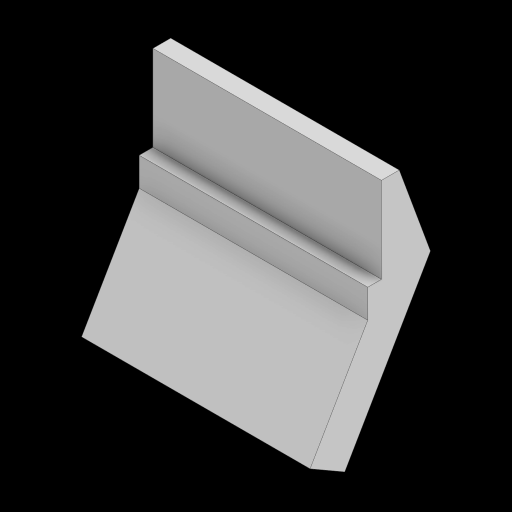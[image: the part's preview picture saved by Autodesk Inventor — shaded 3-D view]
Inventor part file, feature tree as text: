
AUTODESK INVENTOR PART (.ipt)
format: ipt  version: 2024 (Build 280153000, 153)  size: 113,152 bytes
history: native  units: in
note: dims shown in document units (in); Inventor stores cm internally (conversion verified against a paired STEP export)
features: extrude x1, sketch x1
ambient origin geometry x8: Origin, YZ Plane, XZ Plane, XY Plane, X Axis, Y Axis, Z Axis, Center Point
bodies: Solid1 (feature_tree)
feature tree (2):
  extrude  "Extrusion1"  Depth=0.35in
  sketch  "Sketch1"  dims[d0=1.5in d1=0.35in d2=30.0deg d3=0.75in d5=0.12in d6=0.1374in d7=0.25in d9=2.0in d10=0.0in]
